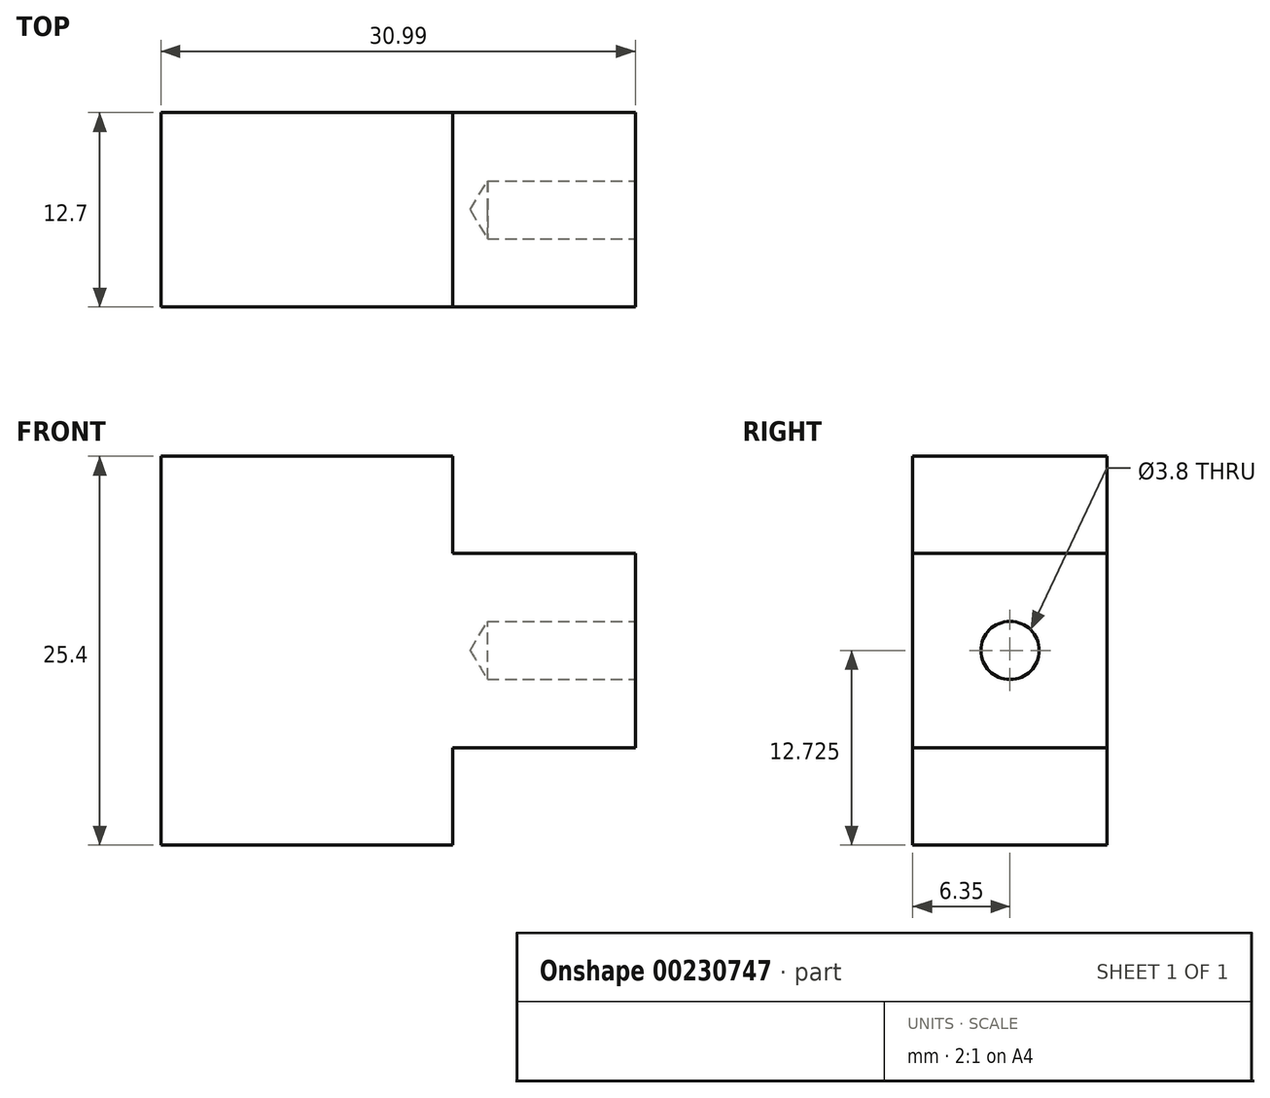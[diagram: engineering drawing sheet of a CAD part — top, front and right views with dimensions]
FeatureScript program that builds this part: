
annotation { "Feature Type Name" : "Feature", "Feature Type Description" : "" }
export const myFeature = defineFeature(function(context is Context, id is Id, definition is map)
    precondition{}
    {
        {
            var Q0;
            Q0=qCreatedBy(makeId("Front.planeOp"),FACE);
            var sketch = newSketch(context, id + "F0", { "sketchPlane" : qUnion([Q0])});
            skLineSegment(sketch, "E0", {"start": v(0, 0) * mm, "end": v(0, 25.4) * mm});
            skLineSegment(sketch, "E1", {"start": v(0, 25.4) * mm, "end": v(19.05, 25.4) * mm});
            skLineSegment(sketch, "E2", {"start": v(19.05, 25.4) * mm, "end": v(19.05, 19.05) * mm});
            skLineSegment(sketch, "E3", {"start": v(19.05, 19.05) * mm, "end": v(30.99, 19.05) * mm});
            skLineSegment(sketch, "E4", {"start": v(30.99, 19.05) * mm, "end": v(30.99, 6.38) * mm});
            skLineSegment(sketch, "E5", {"start": v(30.99, 6.38) * mm, "end": v(19.05, 6.38) * mm});
            skLineSegment(sketch, "E6", {"start": v(19.05, 6.38) * mm, "end": v(19.05, 0) * mm});
            skLineSegment(sketch, "E7", {"start": v(19.05, 0) * mm, "end": v(0, 0) * mm});
            skSolve(sketch);
        }
        {
            var Q0;
            Q0 = qSketchRegion(id + "F0", true);
            extrude(context, id + "F1", {"entities" : qUnion([Q0]), "depth" : 12.7 * mm});
        }
        {
            var Q0;
            Q0=makeQuery(id+"F1.opExtrude","SWEPT_FACE",FACE,{"disambiguationData":[OSD([sQuery(id+"F0.wireOp",EDGE,"E4")])]});
            var sketch = newSketch(context, id + "F2", { "sketchPlane" : qUnion([Q0])});
            skLineSegment(sketch, "E8", {"start": v(-6.35, 6.38) * mm, "end": v(-6.35, 12.73) * mm});
            skPoint(sketch, "E9", {"position": v(-6.35, 12.73) * mm});
            skSolve(sketch);
        }
        {
            var Q0;
            Q0=sQuery(id+"F2.wireOp",VERTEX,"E9");
            var Q1;
            Q1=makeQuery(id+"F1.opExtrude","SWEPT_BODY",BODY,{"disambiguationData":[OSD([sQuery(id+"F0.wireOp",EDGE,"E0"),sQuery(id+"F0.wireOp",EDGE,"E1"),sQuery(id+"F0.wireOp",EDGE,"E2"),sQuery(id+"F0.wireOp",EDGE,"E3"),sQuery(id+"F0.wireOp",EDGE,"E4"),sQuery(id+"F0.wireOp",EDGE,"E5"),sQuery(id+"F0.wireOp",EDGE,"E6"),sQuery(id+"F0.wireOp",EDGE,"E7")])]});
            hole(context, id + "F3", {"style" : HoleStyle.SIMPLE, "endStyle" : HoleEndStyle.BLIND, "standardTappedOrClearance" : lookupTablePath({ "standard" : "ANSI", "engagement" : "75%", "pitch" : "24 tpi", "size" : "#10", "type" : "Tapped" }), "standardBlindInLast" : lookupTablePath({ "standard" : "ANSI", "engagement" : "75%", "pitch" : "24 tpi", "size" : "#10", "type" : "Tapped" }), "holeDiameter" : 3.8 * mm, "holeDepth" : 9.65 * mm, "locations" : qUnion([Q0]), "scope" : qUnion([Q1]), "majorDiameter" : 4.83 * mm});
        }
    });
